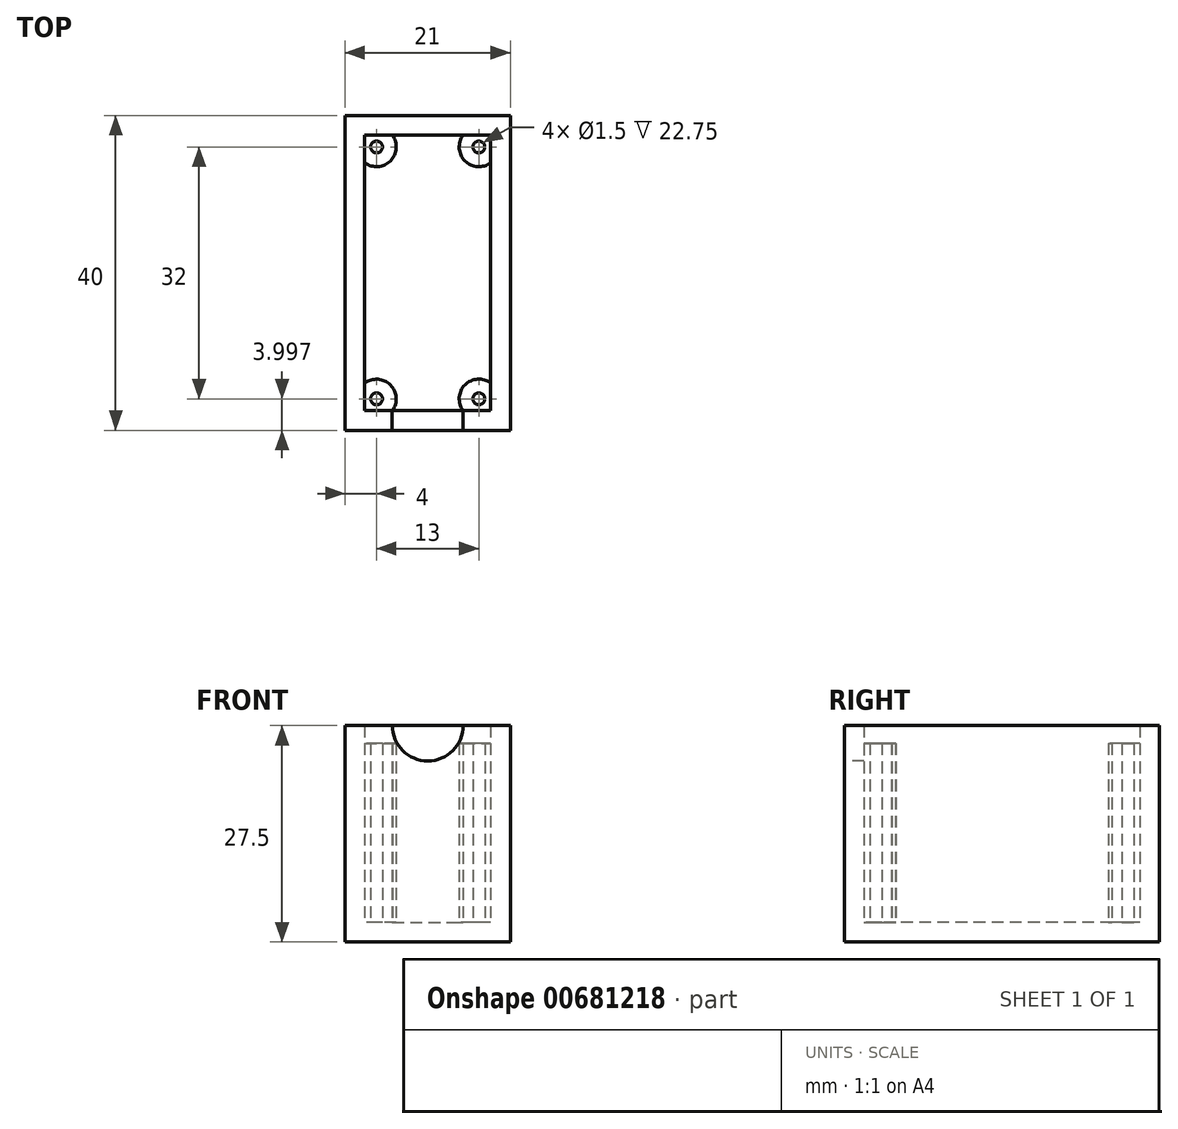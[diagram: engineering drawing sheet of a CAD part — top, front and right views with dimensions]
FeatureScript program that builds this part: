
annotation { "Feature Type Name" : "Feature", "Feature Type Description" : "" }
export const myFeature = defineFeature(function(context is Context, id is Id, definition is map)
    precondition{}
    {
        {
            var Q0;
            Q0=qCreatedBy(makeId("Top.planeOp"),FACE);
            var sketch = newSketch(context, id + "F0", { "sketchPlane" : qUnion([Q0])});
            skLineSegment(sketch, "E0.bottom", {"start": v(-10.5, 20) * mm, "end": v(10.5, 20) * mm});
            skLineSegment(sketch, "E0.top", {"start": v(-10.5, -20) * mm, "end": v(10.5, -20) * mm});
            skLineSegment(sketch, "E0.left", {"start": v(-10.5, 20) * mm, "end": v(-10.5, -20) * mm});
            skLineSegment(sketch, "E0.right", {"start": v(10.5, 20) * mm, "end": v(10.5, -20) * mm});
            skCircle(sketch, "E1", {"center": v(6.5, -16) * mm, "radius": 0.75 * mm});
            skCircle(sketch, "E2", {"center": v(-6.5, -16) * mm, "radius": 0.75 * mm});
            skLineSegment(sketch, "E3.bottom", {"start": v(-8, 17.5) * mm, "end": v(8, 17.5) * mm});
            skLineSegment(sketch, "E3.top", {"start": v(-8, -17.5) * mm, "end": v(8, -17.5) * mm});
            skLineSegment(sketch, "E3.left", {"start": v(-8, 17.5) * mm, "end": v(-8, -17.5) * mm});
            skLineSegment(sketch, "E3.right", {"start": v(8, 17.5) * mm, "end": v(8, -17.5) * mm});
            skCircle(sketch, "E4", {"center": v(-6.5, 16) * mm, "radius": 0.75 * mm});
            skCircle(sketch, "E5", {"center": v(6.5, 16) * mm, "radius": 0.75 * mm});
            skCircle(sketch, "E6", {"center": v(-6.5, 16) * mm, "radius": 2.5 * mm});
            skCircle(sketch, "E7", {"center": v(6.5, 16) * mm, "radius": 2.5 * mm});
            skCircle(sketch, "E8", {"center": v(-6.5, -16) * mm, "radius": 2.5 * mm});
            skCircle(sketch, "E9", {"center": v(6.5, -16) * mm, "radius": 2.5 * mm});
            skSolve(sketch);
        }
        {
            var Q0;
            {var subQ0=sQuery(id+"F0.wireOp",EDGE,"E0.right");var subQ1=sQuery(id+"F0.wireOp",EDGE,"E0.bottom");var subQ2=makeQuery(id+"F0.imprint","INTERSECT",VERTEX,{"derivedFrom":[subQ1,subQ0]});Q0=makeQuery(id+"F0.imprint","IMPRINT",FACE,{"disambiguationData":[TD([[makeQuery(id+"F0.imprint","IMPRINT",EDGE,{"disambiguationData":[TD([[subQ2,1.0]])],"derivedFrom":subQ1}),-1.0]])]});}
            var Q1;
            {var subQ0=sQuery(id+"F0.wireOp",EDGE,"E6");var subQ1=sQuery(id+"F0.wireOp",EDGE,"E0.bottom");var subQ2=makeQuery(id+"F0.imprint","INTERSECT",VERTEX,{"derivedFrom":[subQ1,subQ0]});Q1=makeQuery(id+"F0.imprint","IMPRINT",FACE,{"disambiguationData":[TD([[makeQuery(id+"F0.imprint","IMPRINT",EDGE,{"disambiguationData":[TD([[subQ2,-1.0]])],"derivedFrom":subQ1}),-1.0]])]});}
            var Q2;
            {var subQ0=sQuery(id+"F0.wireOp",EDGE,"E0.left");var subQ1=sQuery(id+"F0.wireOp",EDGE,"E0.bottom");var subQ2=makeQuery(id+"F0.imprint","INTERSECT",VERTEX,{"derivedFrom":[subQ1,subQ0]});Q2=makeQuery(id+"F0.imprint","IMPRINT",FACE,{"disambiguationData":[TD([[makeQuery(id+"F0.imprint","IMPRINT",EDGE,{"disambiguationData":[TD([[subQ2,-1.0]])],"derivedFrom":subQ1}),-1.0]])]});}
            var Q3;
            {var subQ1=sQuery(id+"F0.wireOp",EDGE,"E0.left");var subQ7=sQuery(id+"F0.wireOp",EDGE,"E0.top");var subQ8=makeQuery(id+"F0.imprint","INTERSECT",VERTEX,{"derivedFrom":[subQ7,subQ1]});Q3=makeQuery(id+"F0.imprint","IMPRINT",FACE,{"disambiguationData":[TD([[makeQuery(id+"F0.imprint","IMPRINT",EDGE,{"disambiguationData":[TD([[subQ8,-1.0]])],"derivedFrom":subQ7}),1.0]])]});}
            var Q4;
            {var subQ0=sQuery(id+"F0.wireOp",EDGE,"E8");var subQ1=sQuery(id+"F0.wireOp",EDGE,"E0.top");var subQ2=makeQuery(id+"F0.imprint","INTERSECT",VERTEX,{"derivedFrom":[subQ1,subQ0]});Q4=makeQuery(id+"F0.imprint","IMPRINT",FACE,{"disambiguationData":[TD([[makeQuery(id+"F0.imprint","IMPRINT",EDGE,{"disambiguationData":[TD([[subQ2,-1.0]])],"derivedFrom":subQ1}),1.0]])]});}
            var Q5;
            {var subQ0=sQuery(id+"F0.wireOp",EDGE,"E7");var subQ1=sQuery(id+"F0.wireOp",EDGE,"E0.right");var subQ2=makeQuery(id+"F0.imprint","INTERSECT",VERTEX,{"disambiguationData":[OD(1.0)],"derivedFrom":[subQ1,subQ0]});Q5=makeQuery(id+"F0.imprint","IMPRINT",FACE,{"disambiguationData":[TD([[makeQuery(id+"F0.imprint","IMPRINT",EDGE,{"disambiguationData":[TD([[subQ2,-1.0]])],"derivedFrom":subQ1}),-1.0]])]});}
            var Q6;
            {var subQ0=sQuery(id+"F0.wireOp",EDGE,"E6");var subQ7=sQuery(id+"F0.wireOp",EDGE,"E0.left");var subQ9=makeQuery(id+"F0.imprint","INTERSECT",VERTEX,{"disambiguationData":[OD(0.0)],"derivedFrom":[subQ7,subQ0]});Q6=makeQuery(id+"F0.imprint","IMPRINT",FACE,{"disambiguationData":[TD([[makeQuery(id+"F0.imprint","IMPRINT",EDGE,{"disambiguationData":[TD([[subQ9,-1.0]])],"derivedFrom":subQ7}),1.0]])]});}
            var Q7;
            {var subQ3=sQuery(id+"F0.wireOp",EDGE,"E7");var subQ6=sQuery(id+"F0.wireOp",EDGE,"E0.right");var subQ7=makeQuery(id+"F0.imprint","INTERSECT",VERTEX,{"disambiguationData":[OD(0.0)],"derivedFrom":[subQ6,subQ3]});Q7=makeQuery(id+"F0.imprint","IMPRINT",FACE,{"disambiguationData":[TD([[makeQuery(id+"F0.imprint","IMPRINT",EDGE,{"disambiguationData":[TD([[subQ7,-1.0]])],"derivedFrom":subQ6}),-1.0]])]});}
            var Q8;
            {var subQ0=sQuery(id+"F0.wireOp",EDGE,"E0.right");var subQ1=sQuery(id+"F0.wireOp",EDGE,"E0.top");var subQ2=makeQuery(id+"F0.imprint","INTERSECT",VERTEX,{"derivedFrom":[subQ1,subQ0]});Q8=makeQuery(id+"F0.imprint","IMPRINT",FACE,{"disambiguationData":[TD([[makeQuery(id+"F0.imprint","IMPRINT",EDGE,{"disambiguationData":[TD([[subQ2,1.0]])],"derivedFrom":subQ1}),1.0]])]});}
            var Q9;
            {var subQ0=sQuery(id+"F0.wireOp",EDGE,"E9");var subQ1=sQuery(id+"F0.wireOp",EDGE,"E0.right");var subQ2=makeQuery(id+"F0.imprint","INTERSECT",VERTEX,{"disambiguationData":[OD(0.0)],"derivedFrom":[subQ1,subQ0]});Q9=makeQuery(id+"F0.imprint","IMPRINT",FACE,{"disambiguationData":[TD([[makeQuery(id+"F0.imprint","IMPRINT",EDGE,{"disambiguationData":[TD([[subQ2,-1.0]])],"derivedFrom":subQ1}),-1.0]])]});}
            var Q10;
            {var subQ0=sQuery(id+"F0.wireOp",EDGE,"E3.left");var subQ1=sQuery(id+"F0.wireOp",EDGE,"E3.top");var subQ2=makeQuery(id+"F0.imprint","INTERSECT",VERTEX,{"derivedFrom":[subQ1,subQ0]});Q10=makeQuery(id+"F0.imprint","IMPRINT",FACE,{"disambiguationData":[TD([[makeQuery(id+"F0.imprint","IMPRINT",EDGE,{"disambiguationData":[TD([[subQ2,-1.0]])],"derivedFrom":subQ1}),-1.0]])]});}
            var Q11;
            {var subQ0=sQuery(id+"F0.wireOp",EDGE,"E3.left");var subQ1=sQuery(id+"F0.wireOp",EDGE,"E3.bottom");var subQ2=makeQuery(id+"F0.imprint","INTERSECT",VERTEX,{"derivedFrom":[subQ1,subQ0]});Q11=makeQuery(id+"F0.imprint","IMPRINT",FACE,{"disambiguationData":[TD([[makeQuery(id+"F0.imprint","IMPRINT",EDGE,{"disambiguationData":[TD([[subQ2,-1.0]])],"derivedFrom":subQ1}),1.0]])]});}
            var Q12;
            {var subQ0=sQuery(id+"F0.wireOp",EDGE,"E3.right");var subQ1=sQuery(id+"F0.wireOp",EDGE,"E3.bottom");var subQ2=makeQuery(id+"F0.imprint","INTERSECT",VERTEX,{"derivedFrom":[subQ1,subQ0]});Q12=makeQuery(id+"F0.imprint","IMPRINT",FACE,{"disambiguationData":[TD([[makeQuery(id+"F0.imprint","IMPRINT",EDGE,{"disambiguationData":[TD([[subQ2,1.0]])],"derivedFrom":subQ1}),1.0]])]});}
            var Q13;
            {var subQ0=sQuery(id+"F0.wireOp",EDGE,"E3.right");var subQ1=sQuery(id+"F0.wireOp",EDGE,"E3.top");var subQ2=makeQuery(id+"F0.imprint","INTERSECT",VERTEX,{"derivedFrom":[subQ1,subQ0]});Q13=makeQuery(id+"F0.imprint","IMPRINT",FACE,{"disambiguationData":[TD([[makeQuery(id+"F0.imprint","IMPRINT",EDGE,{"disambiguationData":[TD([[subQ2,1.0]])],"derivedFrom":subQ1}),-1.0]])]});}
            var Q14;
            Q14=sQuery(id+"F0.wireOp",EDGE,"E0.bottom");
            var Q15;
            Q15=sQuery(id+"F0.wireOp",EDGE,"E0.right");
            var Q16;
            Q16=sQuery(id+"F0.wireOp",EDGE,"E0.top");
            var Q17;
            Q17=sQuery(id+"F0.wireOp",EDGE,"E0.left");
            extrude(context, id + "F1", {"entities" : qUnion([Q0, Q1, Q2, Q3, Q4, Q5, Q6, Q7, Q8, Q9, Q10, Q11, Q12, Q13]), "surfaceEntities" : qUnion([Q14, Q15, Q16, Q17]), "depth" : 25 * mm, "offsetDistance" : 25 * mm});
        }
        {
            var Q0;
            Q0=makeQuery(id+"F0.imprint","IMPRINT",FACE,{"disambiguationData":[TD([[makeQuery(id+"F0.imprint","IMPRINT",EDGE,{"derivedFrom":sQuery(id+"F0.wireOp",EDGE,"E4")}),-1.0]])]});
            var Q1;
            Q1=makeQuery(id+"F0.imprint","IMPRINT",FACE,{"disambiguationData":[TD([[makeQuery(id+"F0.imprint","IMPRINT",EDGE,{"derivedFrom":sQuery(id+"F0.wireOp",EDGE,"E5")}),-1.0]])]});
            var Q2;
            Q2=makeQuery(id+"F0.imprint","IMPRINT",FACE,{"disambiguationData":[TD([[makeQuery(id+"F0.imprint","IMPRINT",EDGE,{"derivedFrom":sQuery(id+"F0.wireOp",EDGE,"E1")}),-1.0]])]});
            var Q3;
            Q3=makeQuery(id+"F0.imprint","IMPRINT",FACE,{"disambiguationData":[TD([[makeQuery(id+"F0.imprint","IMPRINT",EDGE,{"derivedFrom":sQuery(id+"F0.wireOp",EDGE,"E2")}),-1.0]])]});
            extrude(context, id + "F2", {"entities" : qUnion([Q0, Q1, Q2, Q3]), "operationType" : NewBodyOperationType.ADD, "depth" : 22.75 * mm, "offsetDistance" : 25 * mm});
        }
        {
            var Q0;
            {var subQ0=sQuery(id+"F0.wireOp",EDGE,"E7");var subQ1=sQuery(id+"F0.wireOp",EDGE,"E0.right");var subQ2=makeQuery(id+"F0.imprint","INTERSECT",VERTEX,{"disambiguationData":[OD(1.0)],"derivedFrom":[subQ1,subQ0]});Q0=makeQuery(id+"F0.imprint","IMPRINT",FACE,{"disambiguationData":[TD([[makeQuery(id+"F0.imprint","IMPRINT",EDGE,{"disambiguationData":[TD([[subQ2,-1.0]])],"derivedFrom":subQ1}),-1.0]])]});}
            var sketch = newSketch(context, id + "F3", { "sketchPlane" : qUnion([Q0])});
            skLineSegment(sketch, "E10.bottom", {"start": v(-10.5, 20) * mm, "end": v(10.5, 20) * mm});
            skLineSegment(sketch, "E10.top", {"start": v(-10.5, -20) * mm, "end": v(10.5, -20) * mm});
            skLineSegment(sketch, "E10.left", {"start": v(-10.5, 20) * mm, "end": v(-10.5, -20) * mm});
            skLineSegment(sketch, "E10.right", {"start": v(10.5, 20) * mm, "end": v(10.5, -20) * mm});
            skSolve(sketch);
        }
        {
            var Q0;
            Q0 = qSketchRegion(id + "F3", true);
            extrude(context, id + "F4", {"entities" : qUnion([Q0]), "operationType" : NewBodyOperationType.ADD, "oppositeDirection" : true, "depth" : 2.5 * mm, "offsetDistance" : 25 * mm});
        }
        {
            var Q0;
            Q0=makeQuery(id+"F4.boolean.opBoolean","MERGE",FACE,{"derivedFrom":[makeQuery(id+"F1.opExtrude","SWEPT_FACE",FACE,{"disambiguationData":[OSD([sQuery(id+"F0.wireOp",EDGE,"E0.top")])]}),makeQuery(id+"F4.opExtrude","SWEPT_FACE",FACE,{"disambiguationData":[OSD([sQuery(id+"F3.wireOp",EDGE,"E10.top")])]})]});
            var sketch = newSketch(context, id + "F5", { "sketchPlane" : qUnion([Q0])});
            skPoint(sketch, "E11", {"position": v(-4.5, 25) * mm});
            skPoint(sketch, "E12", {"position": v(4.5, 25) * mm});
            skCircle(sketch, "E13", {"center": v(0, 25) * mm, "radius": 4.5 * mm});
            skSolve(sketch);
        }
        {
            var Q0;
            Q0 = qSketchRegion(id + "F5", true);
            extrude(context, id + "F6", {"entities" : qUnion([Q0]), "operationType" : NewBodyOperationType.REMOVE, "oppositeDirection" : true, "depth" : 2.5 * mm, "offsetDistance" : 25 * mm});
        }
    });
